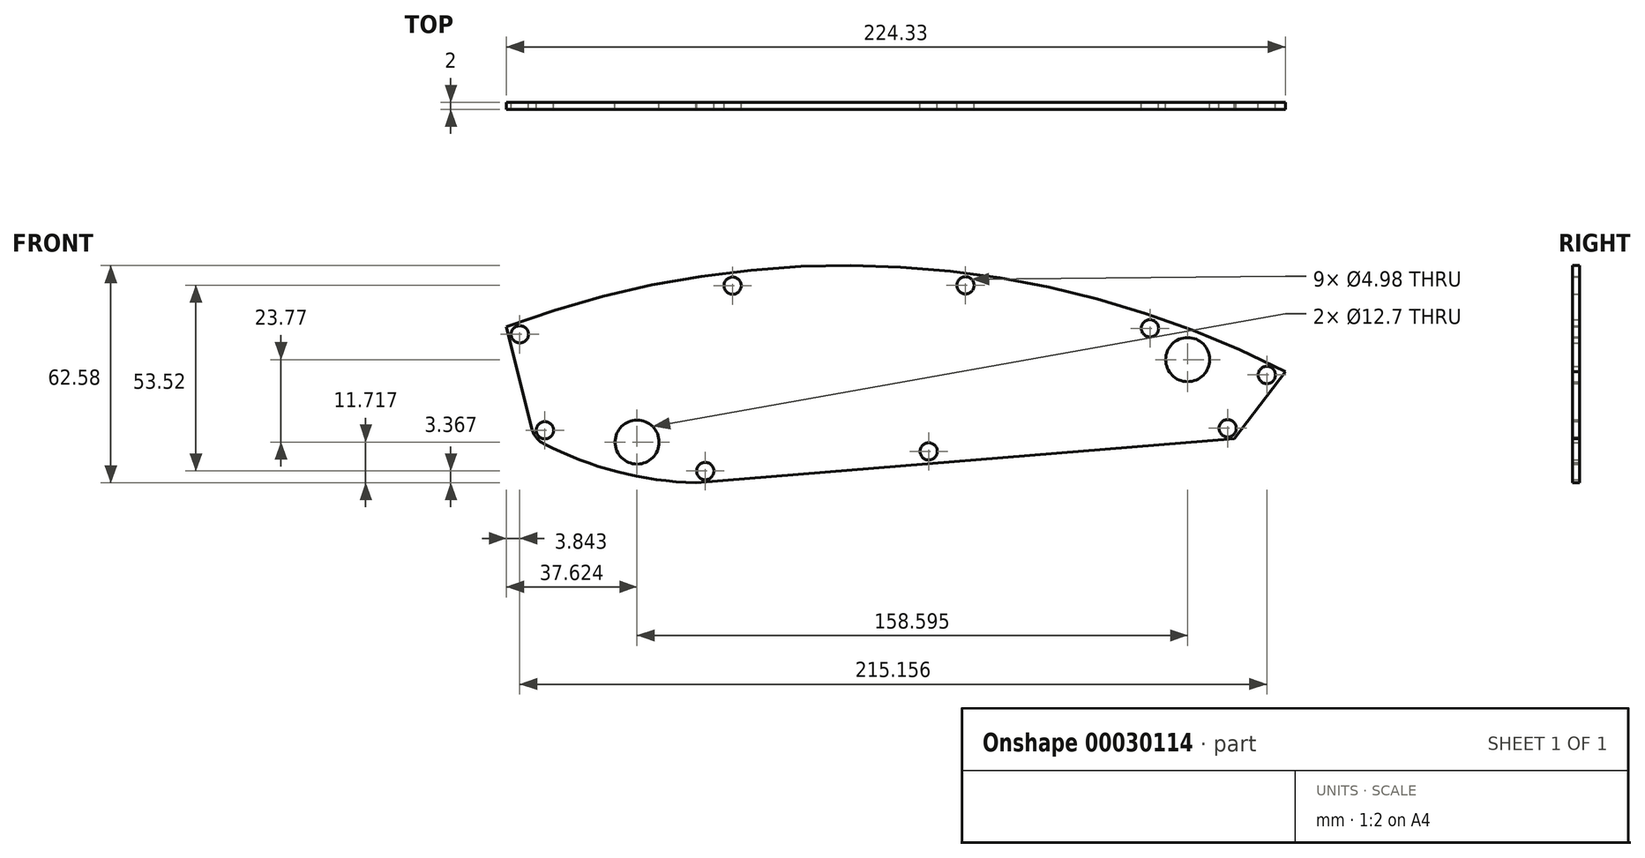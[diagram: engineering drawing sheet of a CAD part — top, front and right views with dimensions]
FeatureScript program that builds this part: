
annotation { "Feature Type Name" : "Feature", "Feature Type Description" : "" }
export const myFeature = defineFeature(function(context is Context, id is Id, definition is map)
    precondition{}
    {
        {
            var Q0;
            Q0=qCreatedBy(makeId("Front.planeOp"),FACE);
            var sketch = newSketch(context, id + "F0", { "sketchPlane" : qUnion([Q0])});
            skLineSegment(sketch, "E0", {"start": v(24.02, -2.26) * mm, "end": v(24.02, -27.66) * mm, "construction": true});
            skLineSegment(sketch, "E1", {"start": v(70.5, -2.26) * mm, "end": v(70.5, -24.49) * mm, "construction": true});
            skLineSegment(sketch, "E2", {"start": v(70.5, -40.36) * mm, "end": v(70.5, -24.49) * mm, "construction": true});
            skPoint(sketch, "E3.visualSharp", {"position": v(24.02, -27.66) * mm});
            skLineSegment(sketch, "E4", {"start": v(15.97, 4.56) * mm, "end": v(23.34, -24.94) * mm});
            skArc(sketch, "E5", {"start": v(26.58, -29.03) * mm, "mid": v(47.9, -37.2) * mm, "end": v(70.5, -40.36) * mm});
            skLineSegment(sketch, "E6", {"start": v(70.5, -40.36) * mm, "end": v(225.56, -27.61) * mm});
            skLineSegment(sketch, "E7", {"start": v(-94.1, -40.36) * mm, "end": v(70.5, -40.36) * mm, "construction": true});
            skLineSegment(sketch, "E8", {"start": v(225.56, -27.61) * mm, "end": v(240.3, -27.61) * mm, "construction": true});
            skLineSegment(sketch, "E9", {"start": v(240.3, -27.61) * mm, "end": v(240.3, -8.3) * mm, "construction": true});
            skArc(sketch, "E10.filletArc", {"start": v(23.34, -24.94) * mm, "mid": v(24.52, -27.33) * mm, "end": v(26.58, -29.03) * mm});
            skArc(sketch, "E11", {"start": v(240.3, -8.3) * mm, "mid": v(129.49, 21.77) * mm, "end": v(15.97, 4.56) * mm});
            skCircle(sketch, "E12", {"center": v(27.05, -25.25) * mm, "radius": 2.49 * mm});
            skCircle(sketch, "E13", {"center": v(19.81, 2.4) * mm, "radius": 2.49 * mm});
            skLineSegment(sketch, "E14", {"start": v(24.02, -2.26) * mm, "end": v(70.5, -2.26) * mm, "construction": true});
            skCircle(sketch, "E15", {"center": v(212.19, -4.87) * mm, "radius": 6.35 * mm});
            skCircle(sketch, "E16", {"center": v(53.6, -28.64) * mm, "radius": 6.35 * mm});
            skLineSegment(sketch, "E17", {"start": v(53.6, -28.64) * mm, "end": v(16.34, 73.72) * mm, "construction": true});
            skLineSegment(sketch, "E18", {"start": v(53.6, -28.64) * mm, "end": v(53.6, -17.8) * mm, "construction": true});
            skLineSegment(sketch, "E19", {"start": v(212.19, -4.87) * mm, "end": v(212.19, -0.97) * mm, "construction": true});
            skLineSegment(sketch, "E20", {"start": v(212.19, -4.87) * mm, "end": v(177.57, 90.24) * mm, "construction": true});
            skLineSegment(sketch, "E21", {"start": v(225.56, -27.61) * mm, "end": v(240.3, -8.3) * mm});
            skCircle(sketch, "E22", {"center": v(73.24, -37) * mm, "radius": 2.49 * mm});
            skCircle(sketch, "E23", {"center": v(223.69, -24.67) * mm, "radius": 2.49 * mm});
            skCircle(sketch, "E24", {"center": v(234.97, -9.3) * mm, "radius": 2.49 * mm});
            skCircle(sketch, "E25", {"center": v(201.31, 4.13) * mm, "radius": 2.49 * mm});
            skCircle(sketch, "E26", {"center": v(148.19, 16.53) * mm, "radius": 2.49 * mm});
            skCircle(sketch, "E27", {"center": v(81.1, 16.43) * mm, "radius": 2.49 * mm});
            skCircle(sketch, "E28", {"center": v(137.58, -31.33) * mm, "radius": 2.49 * mm});
            skSolve(sketch);
        }
        {
            var Q0;
            Q0 = qSketchRegion(id + "F0", true);
            extrude(context, id + "F1", {"entities" : qUnion([Q0]), "depth" : 2 * mm});
        }
    });
